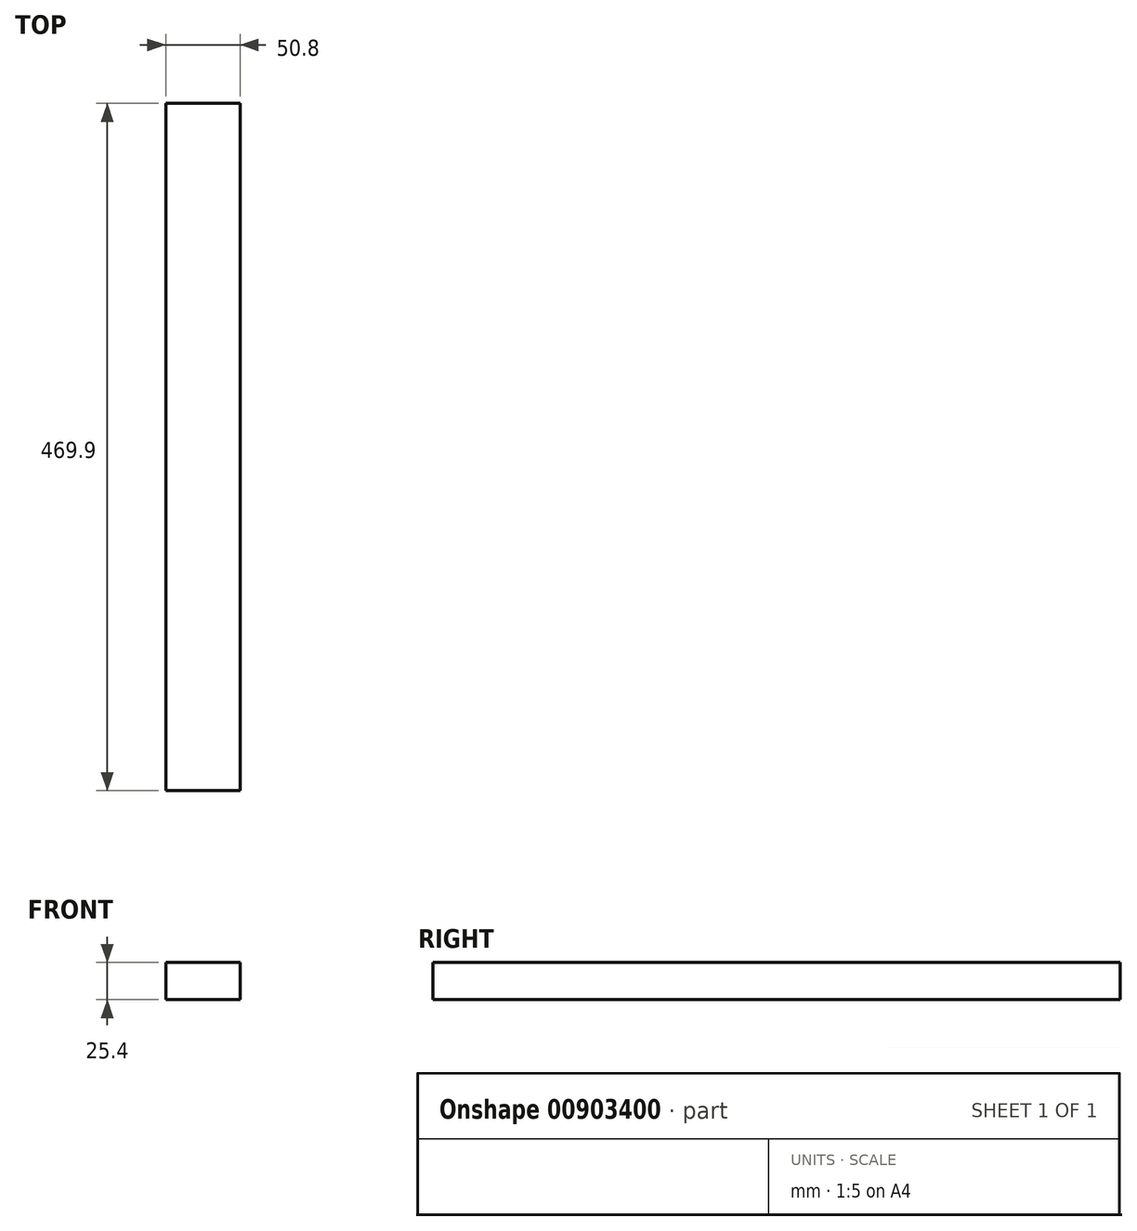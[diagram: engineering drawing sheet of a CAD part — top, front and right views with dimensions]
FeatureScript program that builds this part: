
annotation { "Feature Type Name" : "Feature", "Feature Type Description" : "" }
export const myFeature = defineFeature(function(context is Context, id is Id, definition is map)
    precondition{}
    {
        {
            var Q0;
            Q0=qCreatedBy(makeId("Front.planeOp"),FACE);
            var sketch = newSketch(context, id + "F0", { "sketchPlane" : qUnion([Q0])});
            skLineSegment(sketch, "E0.bottom", {"start": v(0, 0) * mm, "end": v(50.8, 0) * mm});
            skLineSegment(sketch, "E0.top", {"start": v(0, 25.4) * mm, "end": v(50.8, 25.4) * mm});
            skLineSegment(sketch, "E0.left", {"start": v(0, 0) * mm, "end": v(0, 25.4) * mm});
            skLineSegment(sketch, "E0.right", {"start": v(50.8, 0) * mm, "end": v(50.8, 25.4) * mm});
            skSolve(sketch);
        }
        {
            var Q0;
            Q0=makeQuery(id+"F0.imprint","IMPRINT",FACE,{"disambiguationData":[TD([[makeQuery(id+"F0.imprint","IMPRINT",EDGE,{"derivedFrom":sQuery(id+"F0.wireOp",EDGE,"E0.bottom")}),1.0]])]});
            extrude(context, id + "F1", {"entities" : qUnion([Q0]), "depth" : 469.9 * mm, "offsetDistance" : 25.4 * mm});
        }
    });
